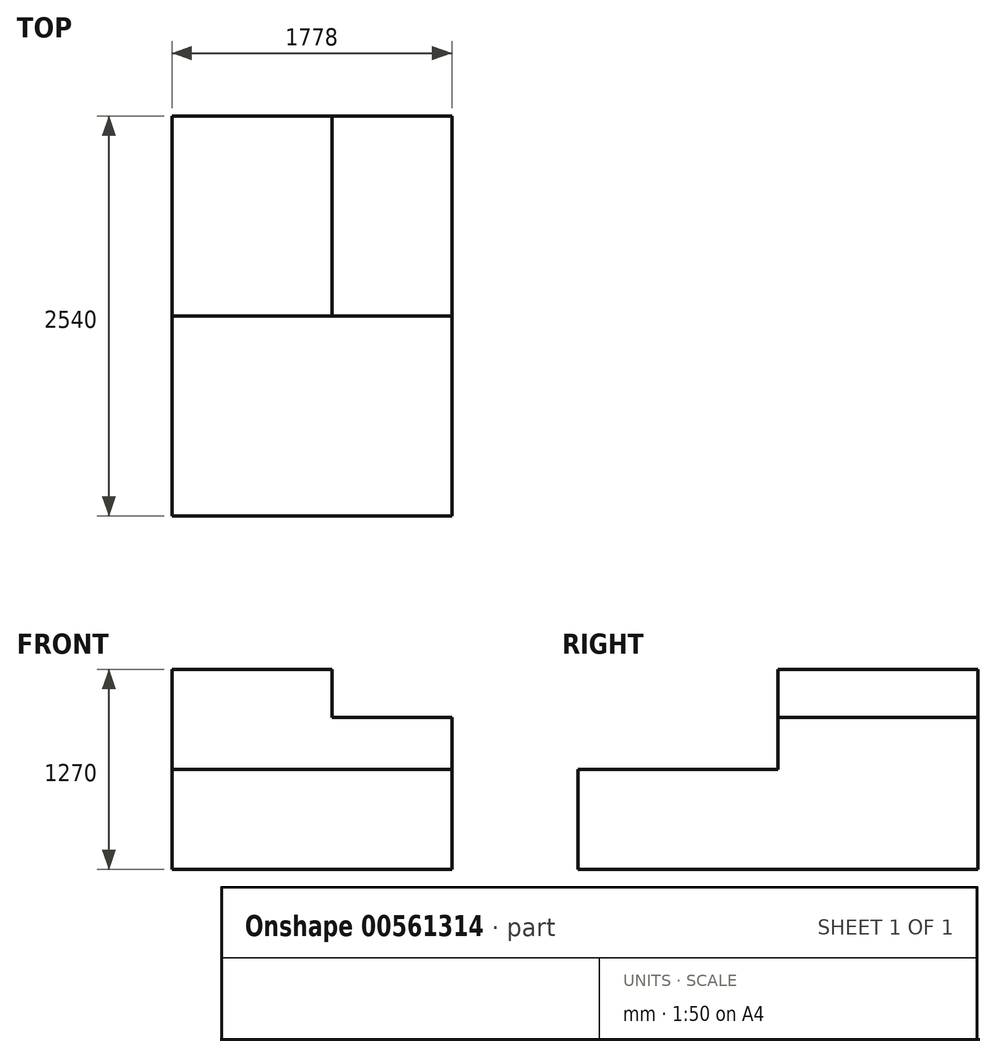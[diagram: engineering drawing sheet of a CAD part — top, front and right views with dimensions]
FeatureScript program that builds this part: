
annotation { "Feature Type Name" : "Feature", "Feature Type Description" : "" }
export const myFeature = defineFeature(function(context is Context, id is Id, definition is map)
    precondition{}
    {
        {
            var Q0;
            Q0=qCreatedBy(makeId("Right.planeOp"),FACE);
            var sketch = newSketch(context, id + "F0", { "sketchPlane" : qUnion([Q0])});
            skLineSegment(sketch, "E0.bottom", {"start": v(-1270.11, -3.66) * mm, "end": v(1269.89, -3.66) * mm});
            skLineSegment(sketch, "E0.top", {"start": v(-1270.11, -1273.66) * mm, "end": v(1269.89, -1273.66) * mm});
            skLineSegment(sketch, "E0.left", {"start": v(-1270.11, -3.66) * mm, "end": v(-1270.11, -1273.66) * mm});
            skLineSegment(sketch, "E0.right", {"start": v(1269.89, -3.66) * mm, "end": v(1269.89, -1273.66) * mm});
            skSolve(sketch);
        }
        {
            var Q0;
            Q0 = qSketchRegion(id + "F0", true);
            extrude(context, id + "F1", {"entities" : qUnion([Q0]), "depth" : 1778 * mm, "offsetDistance" : 25.4 * mm});
        }
        {
            var Q0;
            Q0=makeQuery(id+"F1.opExtrude","SWEPT_FACE",FACE,{"disambiguationData":[OSD([sQuery(id+"F0.wireOp",EDGE,"E0.left")])]});
            var sketch = newSketch(context, id + "F2", { "sketchPlane" : qUnion([Q0])});
            skLineSegment(sketch, "E1", {"start": v(0, -638.66) * mm, "end": v(1778, -638.66) * mm});
            skSolve(sketch);
        }
        {
            var Q0;
            Q0 = qSketchRegion(id + "F2", true);
            var Q1;
            {var subQ0=sQuery(id+"F2.wireOp",EDGE,"E1");Q1=makeQuery(id+"F2.imprint","IMPRINT",FACE,{"disambiguationData":[TD([[makeQuery(id+"F2.imprint","IMPRINT",EDGE,{"derivedFrom":subQ0}),1.0]])]});}
            extrude(context, id + "F3", {"entities" : qUnion([Q0, Q1]), "operationType" : NewBodyOperationType.REMOVE, "oppositeDirection" : true, "depth" : 1270 * mm, "offsetDistance" : 25.4 * mm});
        }
        {
            var Q0;
            Q0=makeQuery(id+"F1.opExtrude","CAP_FACE",FACE,{"disambiguationData":[OSD([sQuery(id+"F0.wireOp",EDGE,"E0.bottom"),sQuery(id+"F0.wireOp",EDGE,"E0.top"),sQuery(id+"F0.wireOp",EDGE,"E0.left"),sQuery(id+"F0.wireOp",EDGE,"E0.right")])],"isStart":false});
            var sketch = newSketch(context, id + "F4", { "sketchPlane" : qUnion([Q0])});
            skLineSegment(sketch, "E2", {"start": v(1269.89, -1273.66) * mm, "end": v(1269.89, -308.46) * mm});
            skLineSegment(sketch, "E3", {"start": v(1269.89, -308.46) * mm, "end": v(-0.11, -308.46) * mm});
            skPoint(sketch, "E3.endSnap0", {"position": v(-0.11, -321.16) * mm});
            skLineSegment(sketch, "E4", {"start": v(-0.11, -638.66) * mm, "end": v(-0.11, -321.16) * mm});
            skSolve(sketch);
        }
        {
            var Q0;
            {var subQ0=sQuery(id+"F4.wireOp",EDGE,"E3");Q0=makeQuery(id+"F4.imprint","IMPRINT",FACE,{"disambiguationData":[TD([[makeQuery(id+"F4.imprint","IMPRINT",EDGE,{"derivedFrom":subQ0}),-1.0]])]});}
            extrude(context, id + "F5", {"entities" : qUnion([Q0]), "operationType" : NewBodyOperationType.REMOVE, "oppositeDirection" : true, "depth" : 762 * mm, "offsetDistance" : 25.4 * mm});
        }
    });
